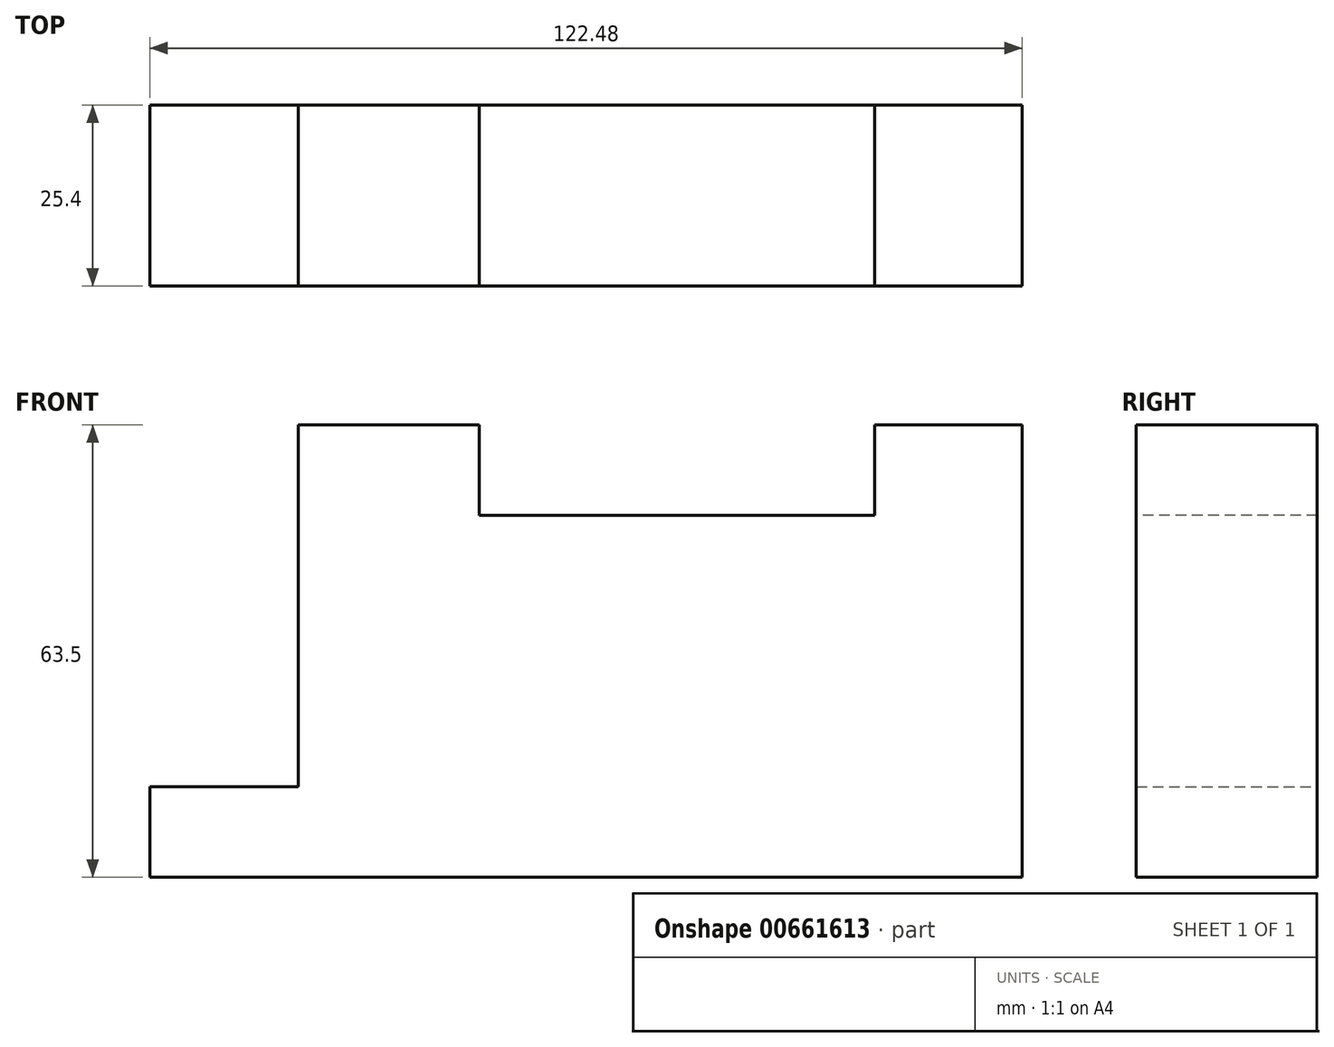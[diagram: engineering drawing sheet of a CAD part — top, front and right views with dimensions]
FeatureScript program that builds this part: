
annotation { "Feature Type Name" : "Feature", "Feature Type Description" : "" }
export const myFeature = defineFeature(function(context is Context, id is Id, definition is map)
    precondition{}
    {
        {
            var Q0;
            Q0=qCreatedBy(makeId("Front.planeOp"),FACE);
            var sketch = newSketch(context, id + "F0", { "sketchPlane" : qUnion([Q0])});
            skLineSegment(sketch, "E0.bottom", {"start": v(-80.86, 66.16) * mm, "end": v(20.74, 66.16) * mm});
            skLineSegment(sketch, "E0.top", {"start": v(-80.86, 15.36) * mm, "end": v(20.74, 15.36) * mm});
            skLineSegment(sketch, "E0.left", {"start": v(-80.86, 66.16) * mm, "end": v(-80.86, 15.36) * mm});
            skLineSegment(sketch, "E0.right", {"start": v(20.74, 66.16) * mm, "end": v(20.74, 15.36) * mm});
            skSolve(sketch);
        }
        {
            var Q0;
            Q0 = qSketchRegion(id + "F0", true);
            extrude(context, id + "F1", {"entities" : qUnion([Q0]), "depth" : 25.4 * mm, "offsetDistance" : 25.4 * mm});
        }
        {
            var Q0;
            Q0=makeQuery(id+"F1.opExtrude","CAP_FACE",FACE,{"disambiguationData":[OSD([sQuery(id+"F0.wireOp",EDGE,"E0.bottom"),sQuery(id+"F0.wireOp",EDGE,"E0.top"),sQuery(id+"F0.wireOp",EDGE,"E0.left"),sQuery(id+"F0.wireOp",EDGE,"E0.right")])],"isStart":false});
            var sketch = newSketch(context, id + "F2", { "sketchPlane" : qUnion([Q0])});
            skLineSegment(sketch, "E1.bottom", {"start": v(-55.46, 66.16) * mm, "end": v(-80.86, 66.16) * mm});
            skLineSegment(sketch, "E1.top", {"start": v(-55.46, 78.86) * mm, "end": v(-80.86, 78.86) * mm});
            skLineSegment(sketch, "E1.left", {"start": v(-55.46, 66.16) * mm, "end": v(-55.46, 78.86) * mm});
            skLineSegment(sketch, "E1.right", {"start": v(-80.86, 66.16) * mm, "end": v(-80.86, 78.86) * mm});
            skSolve(sketch);
        }
        {
            var Q0;
            Q0=makeQuery(id+"F2.imprint","IMPRINT",FACE,{"disambiguationData":[TD([[makeQuery(id+"F2.imprint","IMPRINT",EDGE,{"derivedFrom":sQuery(id+"F2.wireOp",EDGE,"E1.bottom")}),1.0]])]});
            extrude(context, id + "F3", {"entities" : qUnion([Q0]), "operationType" : NewBodyOperationType.ADD, "oppositeDirection" : true, "depth" : 25.4 * mm, "offsetDistance" : 25.4 * mm});
        }
        {
            var Q0;
            Q0=makeQuery(id+"F3.boolean.opBoolean","MERGE",FACE,{"derivedFrom":[makeQuery(id+"F1.opExtrude","CAP_FACE",FACE,{"disambiguationData":[OSD([sQuery(id+"F0.wireOp",EDGE,"E0.bottom"),sQuery(id+"F0.wireOp",EDGE,"E0.top"),sQuery(id+"F0.wireOp",EDGE,"E0.left"),sQuery(id+"F0.wireOp",EDGE,"E0.right")])],"isStart":false}),makeQuery(id+"F3.opExtrude","CAP_FACE",FACE,{"disambiguationData":[OSD([sQuery(id+"F2.wireOp",EDGE,"E1.bottom"),sQuery(id+"F2.wireOp",EDGE,"E1.top"),sQuery(id+"F2.wireOp",EDGE,"E1.left"),sQuery(id+"F2.wireOp",EDGE,"E1.right")])],"isStart":true})]});
            var sketch = newSketch(context, id + "F4", { "sketchPlane" : qUnion([Q0])});
            skLineSegment(sketch, "E2.bottom", {"start": v(20.74, 66.16) * mm, "end": v(0, 66.16) * mm});
            skLineSegment(sketch, "E2.top", {"start": v(20.74, 78.86) * mm, "end": v(0, 78.86) * mm});
            skLineSegment(sketch, "E2.left", {"start": v(20.74, 66.16) * mm, "end": v(20.74, 78.86) * mm});
            skLineSegment(sketch, "E2.right", {"start": v(0, 66.16) * mm, "end": v(0, 78.86) * mm});
            skSolve(sketch);
        }
        {
            var Q0;
            Q0=makeQuery(id+"F4.imprint","IMPRINT",FACE,{"disambiguationData":[TD([[makeQuery(id+"F4.imprint","IMPRINT",EDGE,{"derivedFrom":sQuery(id+"F4.wireOp",EDGE,"E2.bottom")}),1.0]])]});
            extrude(context, id + "F5", {"entities" : qUnion([Q0]), "operationType" : NewBodyOperationType.ADD, "oppositeDirection" : true, "depth" : 25.4 * mm, "offsetDistance" : 25.4 * mm});
        }
        {
            var Q0;
            Q0=makeQuery(id+"F5.boolean.opBoolean","MERGE",FACE,{"derivedFrom":[makeQuery(id+"F1.opExtrude","SWEPT_FACE",FACE,{"disambiguationData":[OSD([sQuery(id+"F0.wireOp",EDGE,"E0.right")])]}),makeQuery(id+"F5.opExtrude","SWEPT_FACE",FACE,{"disambiguationData":[OSD([sQuery(id+"F4.wireOp",EDGE,"E2.left")])]})]});
            var sketch = newSketch(context, id + "F6", { "sketchPlane" : qUnion([Q0])});
            skLineSegment(sketch, "E3.bottom", {"start": v(-25.4, 28.06) * mm, "end": v(0, 28.06) * mm});
            skLineSegment(sketch, "E3.top", {"start": v(-25.4, 15.36) * mm, "end": v(0, 15.36) * mm});
            skLineSegment(sketch, "E3.left", {"start": v(-25.4, 28.06) * mm, "end": v(-25.4, 15.36) * mm});
            skLineSegment(sketch, "E3.right", {"start": v(0, 28.06) * mm, "end": v(0, 15.36) * mm});
            skSolve(sketch);
        }
        {
            var Q0;
            Q0=makeQuery(id+"F6.imprint","IMPRINT",FACE,{"disambiguationData":[TD([[makeQuery(id+"F6.imprint","IMPRINT",EDGE,{"derivedFrom":sQuery(id+"F6.wireOp",EDGE,"E3.bottom")}),-1.0]])]});
            extrude(context, id + "F7", {"entities" : qUnion([Q0]), "operationType" : NewBodyOperationType.ADD, "endBound" : BoundingType.THROUGH_ALL, "oppositeDirection" : true, "depth" : 28.2 * mm, "offsetDistance" : 25.4 * mm});
        }
    });
